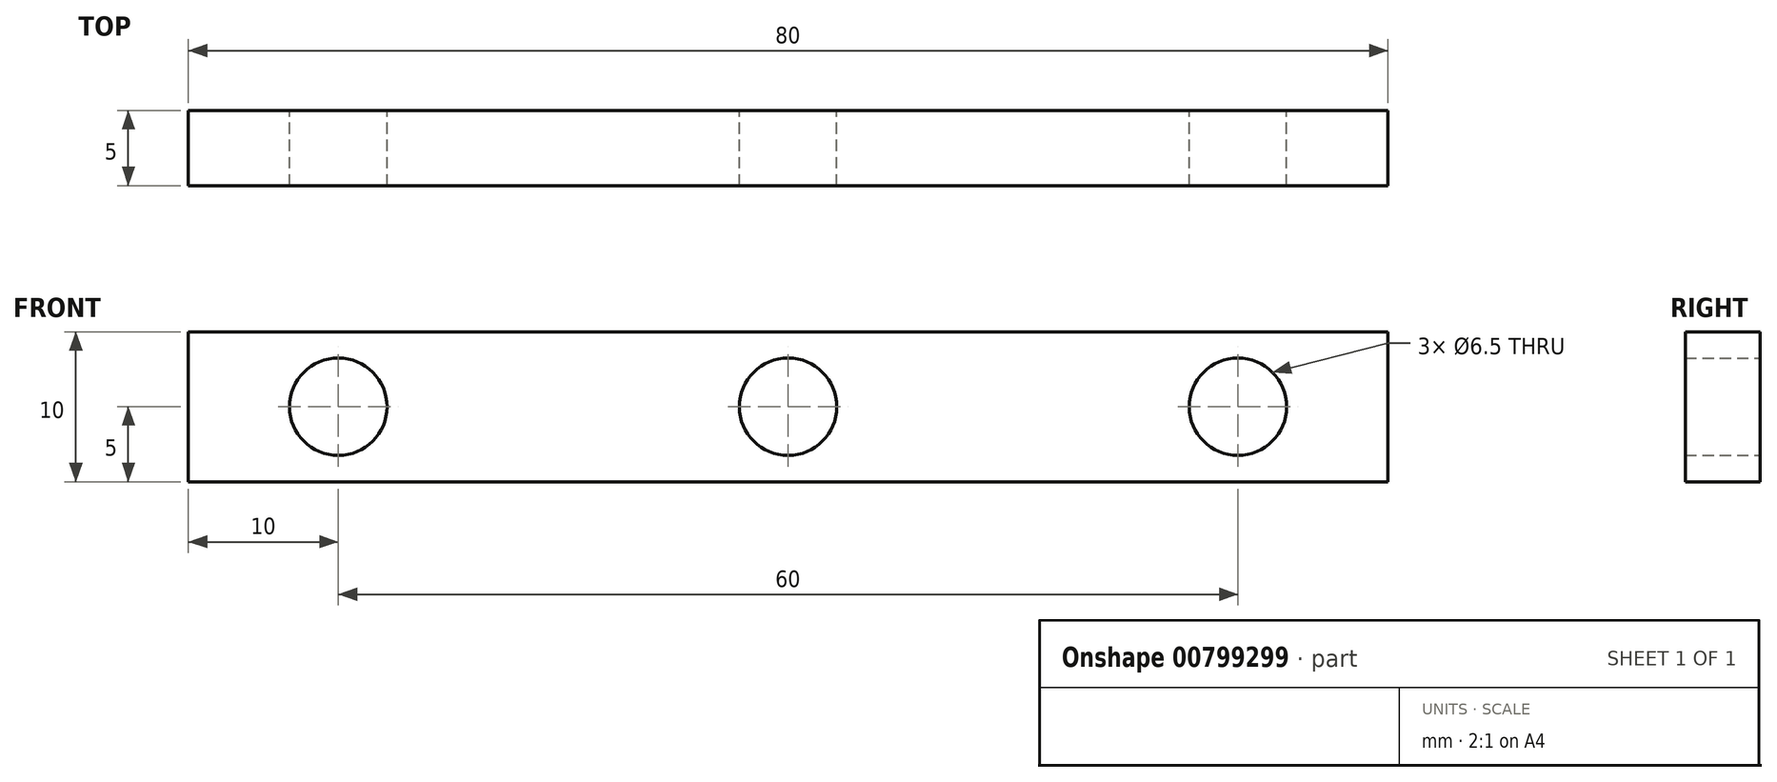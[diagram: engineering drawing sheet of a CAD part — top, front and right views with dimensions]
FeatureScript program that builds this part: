
annotation { "Feature Type Name" : "Feature", "Feature Type Description" : "" }
export const myFeature = defineFeature(function(context is Context, id is Id, definition is map)
    precondition{}
    {
        {
            var Q0;
            Q0=qCreatedBy(makeId("Front.planeOp"),FACE);
            var sketch = newSketch(context, id + "F0", { "sketchPlane" : qUnion([Q0])});
            skLineSegment(sketch, "E0.bottom", {"start": v(-40, 5) * mm, "end": v(40, 5) * mm});
            skLineSegment(sketch, "E0.top", {"start": v(-40, -5) * mm, "end": v(40, -5) * mm});
            skLineSegment(sketch, "E0.left", {"start": v(-40, 5) * mm, "end": v(-40, -5) * mm});
            skLineSegment(sketch, "E0.right", {"start": v(40, 5) * mm, "end": v(40, -5) * mm});
            skPoint(sketch, "E0.middle", {"position": v(0, 0) * mm});
            skCircle(sketch, "E1", {"center": v(0, 0) * mm, "radius": 3.25 * mm});
            skCircle(sketch, "E2", {"center": v(30, 0) * mm, "radius": 3.25 * mm});
            skCircle(sketch, "E3", {"center": v(-30, 0) * mm, "radius": 3.25 * mm});
            skPoint(sketch, "E3.centerSnap0", {"position": v(-40, 0) * mm});
            skSolve(sketch);
        }
        {
            var Q0;
            Q0 = qSketchRegion(id + "F0", true);
            extrude(context, id + "F1", {"entities" : qUnion([Q0]), "depth" : 5 * mm, "offsetDistance" : 25 * mm});
        }
    });
